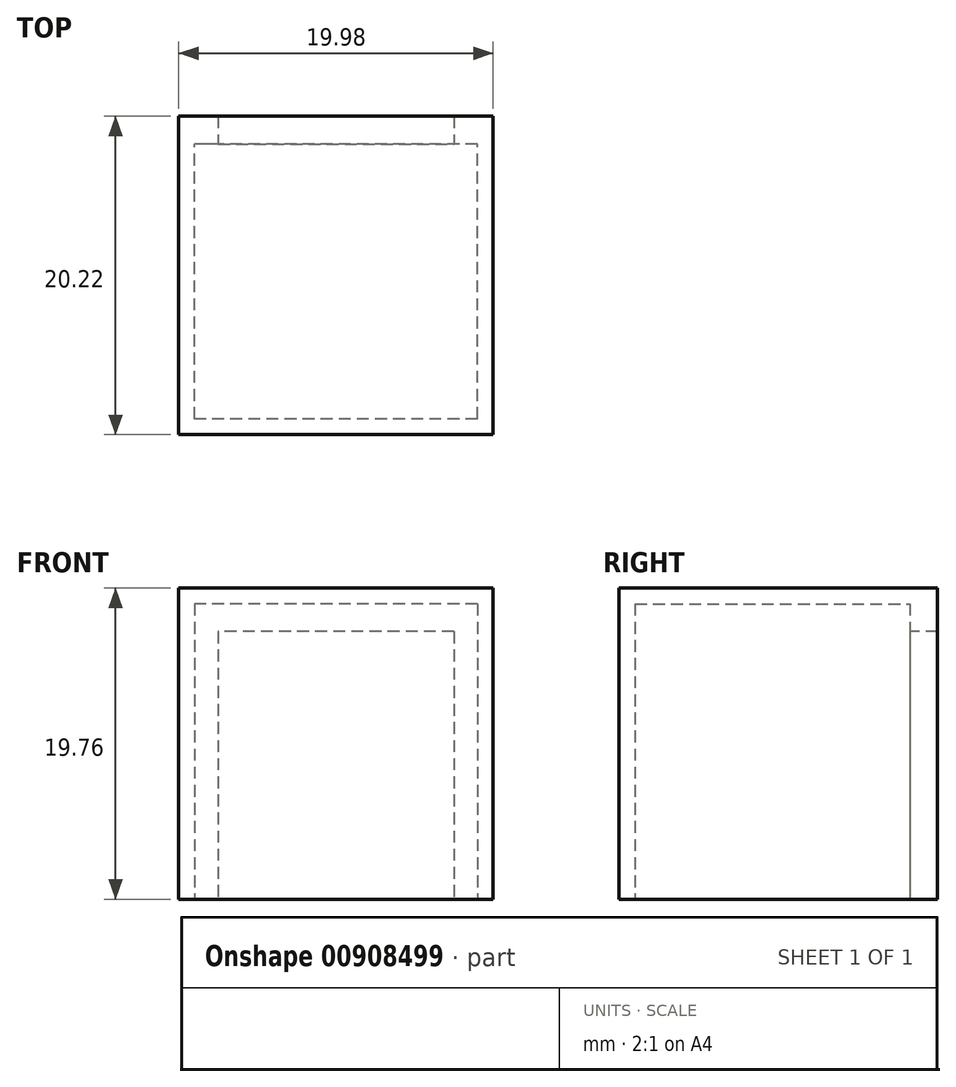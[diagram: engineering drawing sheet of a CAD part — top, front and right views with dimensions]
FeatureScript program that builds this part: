
annotation { "Feature Type Name" : "Feature", "Feature Type Description" : "" }
export const myFeature = defineFeature(function(context is Context, id is Id, definition is map)
    precondition{}
    {
        {
            var Q0;
            Q0=qCreatedBy(makeId("Front.planeOp"),FACE);
            var sketch = newSketch(context, id + "F0", { "sketchPlane" : qUnion([Q0])});
            skLineSegment(sketch, "E0.bottom", {"start": v(9.99, 9.88) * mm, "end": v(-9.98, 9.88) * mm});
            skLineSegment(sketch, "E0.top", {"start": v(9.98, -9.88) * mm, "end": v(-9.99, -9.88) * mm});
            skLineSegment(sketch, "E0.left", {"start": v(9.99, 9.88) * mm, "end": v(9.98, -9.88) * mm});
            skLineSegment(sketch, "E0.right", {"start": v(-9.98, 9.88) * mm, "end": v(-9.99, -9.88) * mm});
            skPoint(sketch, "E0.middle", {"position": v(0, 0) * mm});
            skSolve(sketch);
        }
        {
            var Q0;
            Q0 = qSketchRegion(id + "F0", true);
            extrude(context, id + "F1", {"entities" : qUnion([Q0]), "depth" : 20.22 * mm, "offsetDistance" : 25 * mm});
        }
        {
            var Q0;
            Q0=makeQuery(id+"F1.opExtrude","SWEPT_FACE",FACE,{"disambiguationData":[OSD([sQuery(id+"F0.wireOp",EDGE,"E0.top")])]});
            var sketch = newSketch(context, id + "F2", { "sketchPlane" : qUnion([Q0])});
            skLineSegment(sketch, "E1.0", {"start": v(8.98, 19.22) * mm, "end": v(-8.99, 19.22) * mm});
            skLineSegment(sketch, "E2.0", {"start": v(8.98, 19.22) * mm, "end": v(8.98, 1.75) * mm});
            skLineSegment(sketch, "E3.0", {"start": v(-8.99, 19.22) * mm, "end": v(-8.99, 1.75) * mm});
            skLineSegment(sketch, "E4", {"start": v(8.98, 1.75) * mm, "end": v(7.48, 1.75) * mm});
            skLineSegment(sketch, "E5", {"start": v(8.98, 0) * mm, "end": v(7.48, 0) * mm});
            skLineSegment(sketch, "E6", {"start": v(7.48, 0) * mm, "end": v(7.48, 1.75) * mm});
            skLineSegment(sketch, "E7", {"start": v(-8.99, 0) * mm, "end": v(-7.49, 0) * mm});
            skLineSegment(sketch, "E8", {"start": v(-7.49, 0) * mm, "end": v(-7.49, 1.75) * mm});
            skLineSegment(sketch, "E9", {"start": v(-7.49, 1.75) * mm, "end": v(-8.99, 1.75) * mm});
            skLineSegment(sketch, "E10", {"start": v(-7.49, 1.75) * mm, "end": v(7.48, 1.75) * mm});
            skSolve(sketch);
        }
        {
            var Q0;
            Q0 = qSketchRegion(id + "F2", true);
            var Q1;
            Q1=makeQuery(id+"F2.imprint","IMPRINT",FACE,{"disambiguationData":[TD([[makeQuery(id+"F2.imprint","IMPRINT",EDGE,{"derivedFrom":sQuery(id+"F2.wireOp",EDGE,"E1.0")}),1.0]])]});
            extrude(context, id + "F3", {"entities" : qUnion([Q0, Q1]), "operationType" : NewBodyOperationType.REMOVE, "oppositeDirection" : true, "depth" : 18.76 * mm, "offsetDistance" : 25 * mm});
        }
        {
            var Q0;
            {var subQ0=sQuery(id+"F2.wireOp",EDGE,"E6");Q0=makeQuery(id+"F2.imprint","IMPRINT",FACE,{"disambiguationData":[TD([[makeQuery(id+"F2.imprint","IMPRINT",EDGE,{"derivedFrom":subQ0}),1.0]])]});}
            var Q1;
            Q1=makeQuery(id+"F2.imprint","IMPRINT",FACE,{"disambiguationData":[TD([[makeQuery(id+"F2.imprint","IMPRINT",EDGE,{"derivedFrom":sQuery(id+"F2.wireOp",EDGE,"E1.0")}),1.0]])]});
            extrude(context, id + "F4", {"entities" : qUnion([Q0, Q1]), "operationType" : NewBodyOperationType.REMOVE, "oppositeDirection" : true, "depth" : 17 * mm, "offsetDistance" : 25 * mm});
        }
    });
